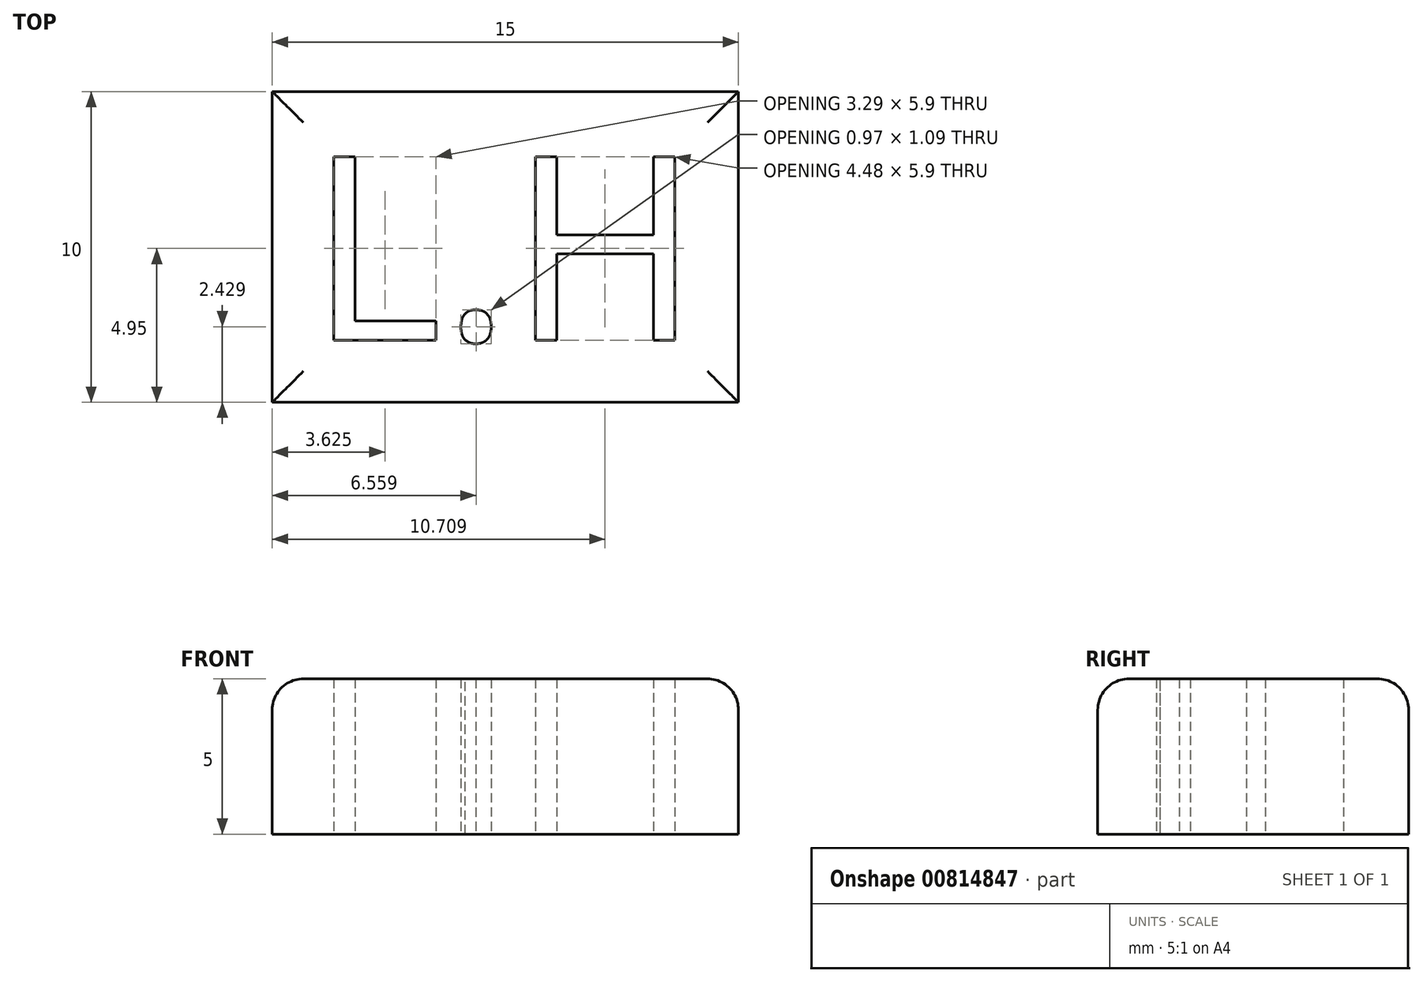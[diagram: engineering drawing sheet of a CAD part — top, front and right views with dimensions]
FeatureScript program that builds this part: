
annotation { "Feature Type Name" : "Feature", "Feature Type Description" : "" }
export const myFeature = defineFeature(function(context is Context, id is Id, definition is map)
    precondition{}
    {
        {
            var Q0;
            Q0=qCreatedBy(makeId("Top.planeOp"),FACE);
            var sketch = newSketch(context, id + "F0", { "sketchPlane" : qUnion([Q0])});
            skLineSegment(sketch, "E0.bottom", {"start": v(-10, -20) * mm, "end": v(-25, -20) * mm});
            skLineSegment(sketch, "E0.top", {"start": v(-10, -10) * mm, "end": v(-25, -10) * mm});
            skLineSegment(sketch, "E0.left", {"start": v(-10, -20) * mm, "end": v(-10, -10) * mm});
            skLineSegment(sketch, "E0.right", {"start": v(-25, -20) * mm, "end": v(-25, -10) * mm});
            skText(sketch, "E1", { "text": "L.H", "fontName": "OpenSans-Regular.ttf"});
            const initialGuessF0  = {"E1": [-0.02383, -0.018, 1, 0, 0.00595]};
            skSetInitialGuess(sketch, initialGuessF0);
            skSolve(sketch);
        }
        {
            var Q0;
            Q0 = qSketchRegion(id + "F0", true);
            extrude(context, id + "F1", {"entities" : qUnion([Q0]), "depth" : 5 * mm, "offsetDistance" : 25 * mm});
        }
        {
            var Q0;
            Q0=makeQuery(id+"F1.opExtrude","CAP_EDGE",EDGE,{"disambiguationData":[OSD([sQuery(id+"F0.wireOp",EDGE,"E0.left")])],"isStart":false});
            var Q1;
            Q1=makeQuery(id+"F1.opExtrude","CAP_EDGE",EDGE,{"disambiguationData":[OSD([sQuery(id+"F0.wireOp",EDGE,"E0.top")])],"isStart":false});
            var Q2;
            Q2=makeQuery(id+"F1.opExtrude","CAP_EDGE",EDGE,{"disambiguationData":[OSD([sQuery(id+"F0.wireOp",EDGE,"E0.bottom")])],"isStart":false});
            var Q3;
            Q3=makeQuery(id+"F1.opExtrude","CAP_EDGE",EDGE,{"disambiguationData":[OSD([sQuery(id+"F0.wireOp",EDGE,"E0.right")])],"isStart":false});
            fillet(context, id + "F2", {"entities" : qUnion([Q0, Q1, Q2, Q3]), "radius" : 1 * mm, "tangentPropagation" : true, "allowEdgeOverflow" : false});
        }
    });
